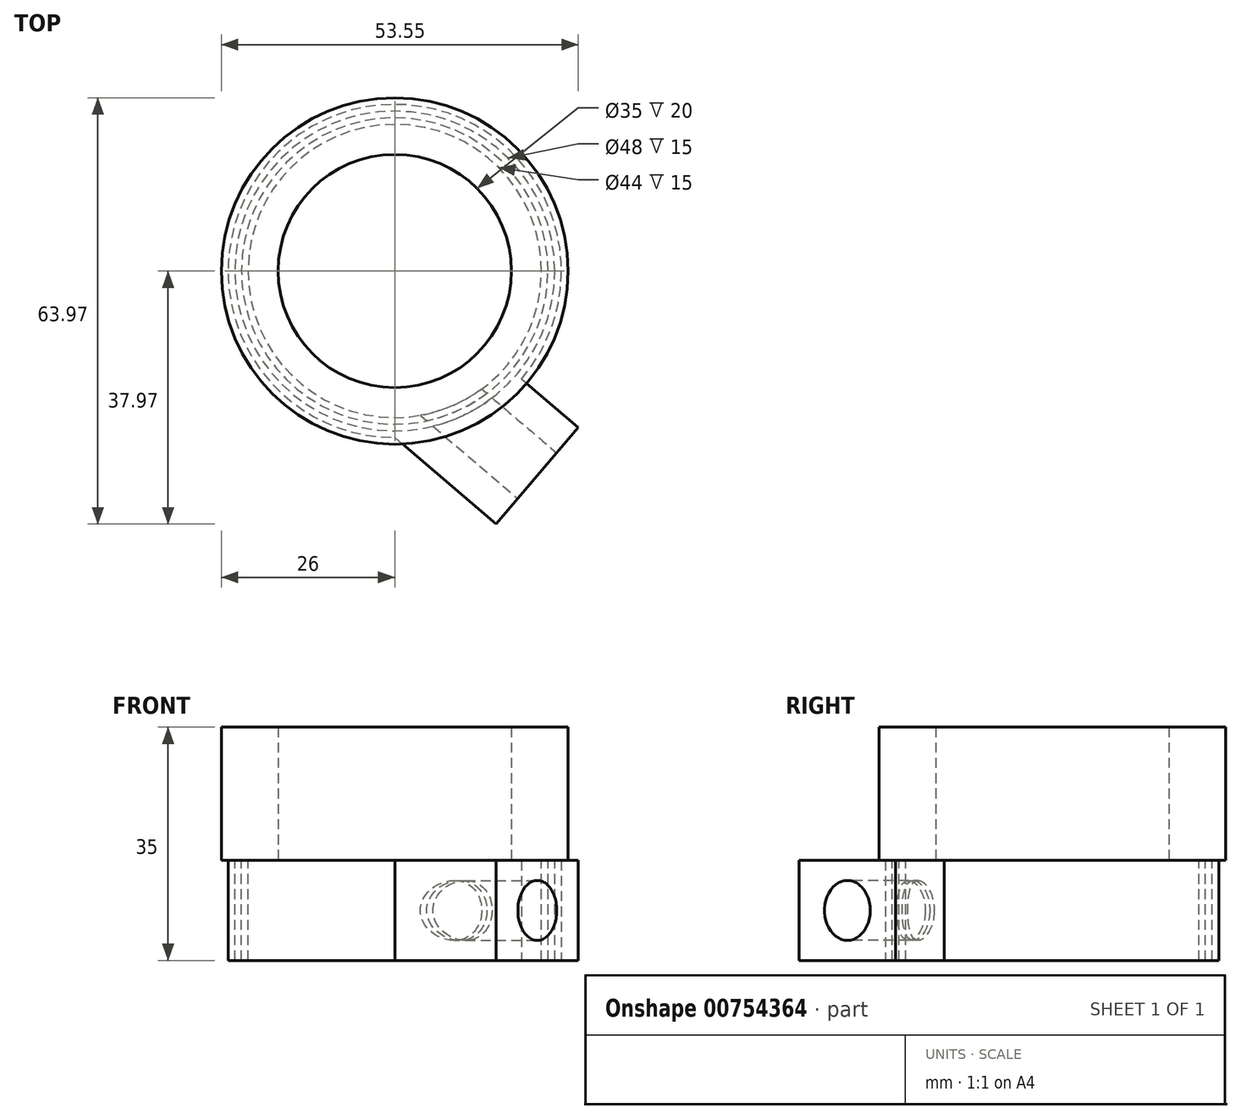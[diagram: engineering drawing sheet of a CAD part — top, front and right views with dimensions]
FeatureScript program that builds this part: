
annotation { "Feature Type Name" : "Feature", "Feature Type Description" : "" }
export const myFeature = defineFeature(function(context is Context, id is Id, definition is map)
    precondition{}
    {
        {
            var Q0;
            Q0=qCreatedBy(makeId("Top.planeOp"),FACE);
            var sketch = newSketch(context, id + "F0", { "sketchPlane" : qUnion([Q0])});
            skArc(sketch, "E0", {"start": v(19.01, -16.24) * mm, "mid": v(-10.47, 22.7) * mm, "end": v(0, -25) * mm});
            skLineSegment(sketch, "E1", {"start": v(0, -25) * mm, "end": v(15.23, -37.97) * mm});
            skLineSegment(sketch, "E2", {"start": v(15.23, -37.97) * mm, "end": v(27.55, -23.5) * mm});
            skLineSegment(sketch, "E3", {"start": v(27.55, -23.5) * mm, "end": v(19.01, -16.24) * mm});
            skSolve(sketch);
        }
        {
            var Q0;
            Q0 = qSketchRegion(id + "F0", true);
            extrude(context, id + "F1", {"entities" : qUnion([Q0]), "depth" : 15 * mm, "offsetDistance" : 25 * mm});
        }
        {
            var Q0;
            Q0=makeQuery(id+"F1.opExtrude","SWEPT_FACE",FACE,{"disambiguationData":[OSD([sQuery(id+"F0.wireOp",EDGE,"E2")])]});
            var sketch = newSketch(context, id + "F2", { "sketchPlane" : qUnion([Q0])});
            skCircle(sketch, "E4", {"center": v(-9.52, 7.5) * mm, "radius": 4.5 * mm});
            skSolve(sketch);
        }
        {
            var Q0;
            Q0 = qSketchRegion(id + "F2", true);
            extrude(context, id + "F3", {"entities" : qUnion([Q0]), "operationType" : NewBodyOperationType.REMOVE, "oppositeDirection" : true, "depth" : 20 * mm, "offsetDistance" : 25 * mm});
        }
        {
            var Q0;
            Q0=makeQuery(id+"F1.opExtrude","CAP_FACE",FACE,{"disambiguationData":[OSD([sQuery(id+"F0.wireOp",EDGE,"E0"),sQuery(id+"F0.wireOp",EDGE,"E1"),sQuery(id+"F0.wireOp",EDGE,"E2"),sQuery(id+"F0.wireOp",EDGE,"E3")])],"isStart":false});
            var sketch = newSketch(context, id + "F4", { "sketchPlane" : qUnion([Q0])});
            skCircle(sketch, "E5", {"center": v(0, 0) * mm, "radius": 22 * mm});
            skSolve(sketch);
        }
        {
            var Q0;
            Q0 = qSketchRegion(id + "F4", true);
            extrude(context, id + "F5", {"entities" : qUnion([Q0]), "operationType" : NewBodyOperationType.REMOVE, "oppositeDirection" : true, "depth" : 15 * mm, "offsetDistance" : 25 * mm});
        }
        {
            var Q0;
            Q0=makeQuery(id+"F4.imprint","IMPRINT",FACE,{"disambiguationData":[TD([[makeQuery(id+"F4.imprint","IMPRINT",EDGE,{"derivedFrom":sQuery(id+"F4.wireOp",EDGE,"E5")}),1.0]])]});
            var sketch = newSketch(context, id + "F6", { "sketchPlane" : qUnion([Q0])});
            skCircle(sketch, "E6", {"center": v(0, 0) * mm, "radius": 24 * mm});
            skCircle(sketch, "E7", {"center": v(0, 0) * mm, "radius": 23 * mm});
            skSolve(sketch);
        }
        {
            var Q0;
            Q0 = qSketchRegion(id + "F6", true);
            extrude(context, id + "F7", {"entities" : qUnion([Q0]), "operationType" : NewBodyOperationType.REMOVE, "oppositeDirection" : true, "depth" : 15 * mm, "offsetDistance" : 25 * mm});
        }
        {
            var Q0;
            Q0=qCreatedBy(makeId("Top.planeOp"),FACE);
            cPlane(context, id + "F8", {"entities" : qUnion([Q0]), "cplaneType" : CPlaneType.OFFSET, "offset" : 15 * mm, "width" : 150 * mm, "height" : 150 * mm});
        }
        {
            var Q0;
            Q0=qCreatedBy(id+"F8.planeOp",FACE);
            var sketch = newSketch(context, id + "F9", { "sketchPlane" : qUnion([Q0])});
            skCircle(sketch, "E8", {"center": v(0, 0) * mm, "radius": 26 * mm});
            skCircle(sketch, "E9", {"center": v(0, 0) * mm, "radius": 17.5 * mm});
            skSolve(sketch);
        }
        {
            var Q0;
            Q0 = qSketchRegion(id + "F9", true);
            extrude(context, id + "F10", {"entities" : qUnion([Q0]), "depth" : 20 * mm, "offsetDistance" : 25 * mm});
        }
    });
